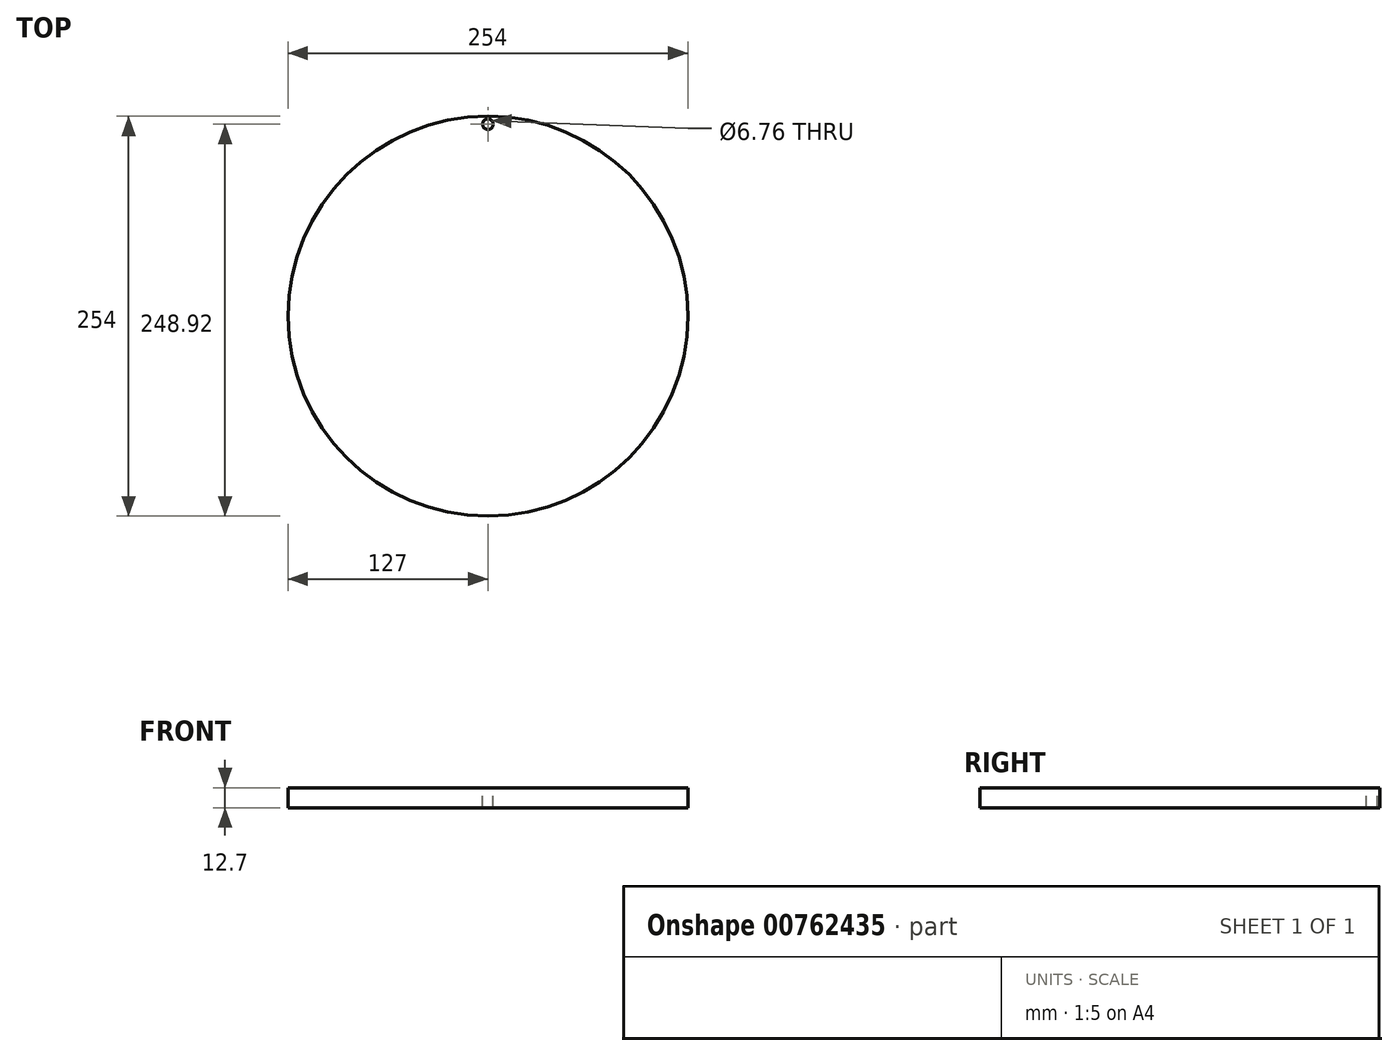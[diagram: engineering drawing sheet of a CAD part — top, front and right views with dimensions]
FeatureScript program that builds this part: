
annotation { "Feature Type Name" : "Feature", "Feature Type Description" : "" }
export const myFeature = defineFeature(function(context is Context, id is Id, definition is map)
    precondition{}
    {
        {
            var Q0;
            Q0=qCreatedBy(makeId("Top.planeOp"),FACE);
            var sketch = newSketch(context, id + "F0", { "sketchPlane" : qUnion([Q0])});
            skCircle(sketch, "E0", {"center": v(0, 0) * mm, "radius": 127 * mm});
            skSolve(sketch);
        }
        {
            var Q0;
            Q0 = qSketchRegion(id + "F0", true);
            extrude(context, id + "F1", {"entities" : qUnion([Q0]), "depth" : 12.7 * mm, "offsetDistance" : 25.4 * mm});
        }
        {
            var Q0;
            Q0=makeQuery(id+"F1.opExtrude","CAP_FACE",FACE,{"disambiguationData":[OSD([sQuery(id+"F0.wireOp",EDGE,"E0")])],"isStart":false});
            var sketch = newSketch(context, id + "F2", { "sketchPlane" : qUnion([Q0])});
            skCircle(sketch, "E1", {"center": v(0, 0) * mm, "radius": 121.92 * mm});
            skCircle(sketch, "E2", {"center": v(0, 121.92) * mm, "radius": 3.38 * mm});
            skCircle(sketch, "E3.1.0", {"center": v(-105.59, -60.96) * mm, "radius": 3.38 * mm});
            skCircle(sketch, "E3.2.0", {"center": v(105.59, -60.96) * mm, "radius": 3.38 * mm});
            skSolve(sketch);
        }
        {
            var Q0;
            {var subQ0=sQuery(id+"F2.wireOp",EDGE,"E2");var subQ1=sQuery(id+"F2.wireOp",EDGE,"E1");var subQ2=makeQuery(id+"F2.imprint","INTERSECT",VERTEX,{"disambiguationData":[OD(0.0)],"derivedFrom":[subQ1,subQ0]});Q0=makeQuery(id+"F2.imprint","IMPRINT",FACE,{"disambiguationData":[TD([[makeQuery(id+"F2.imprint","IMPRINT",EDGE,{"disambiguationData":[TD([[subQ2,1.0]])],"derivedFrom":subQ1}),1.0]])]});}
            var Q1;
            {var subQ0=sQuery(id+"F2.wireOp",EDGE,"E2");var subQ1=sQuery(id+"F2.wireOp",EDGE,"E1");var subQ2=makeQuery(id+"F2.imprint","INTERSECT",VERTEX,{"disambiguationData":[OD(0.0)],"derivedFrom":[subQ1,subQ0]});Q1=makeQuery(id+"F2.imprint","IMPRINT",FACE,{"disambiguationData":[TD([[makeQuery(id+"F2.imprint","IMPRINT",EDGE,{"disambiguationData":[TD([[subQ2,1.0]])],"derivedFrom":subQ1}),-1.0]])]});}
            extrude(context, id + "F3", {"entities" : qUnion([Q0, Q1]), "operationType" : NewBodyOperationType.REMOVE, "endBound" : BoundingType.THROUGH_ALL, "oppositeDirection" : true, "depth" : 25.4 * mm, "offsetDistance" : 25.4 * mm});
        }
    });
